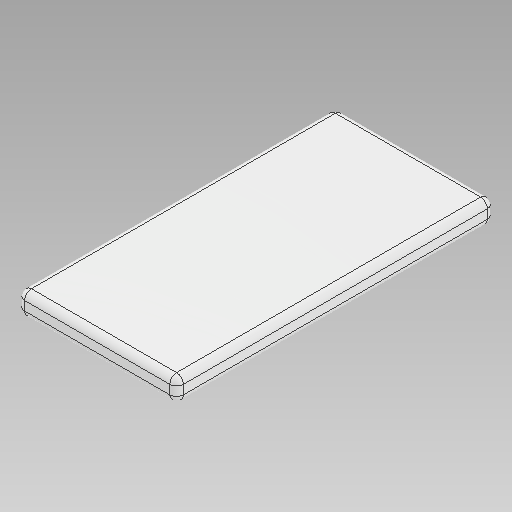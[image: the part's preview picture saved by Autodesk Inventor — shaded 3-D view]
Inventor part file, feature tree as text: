
AUTODESK INVENTOR PART (.ipt)
format: ipt  version: 2020 (Build 240168000, 168)  size: 187,904 bytes
history: native  units: in
note: dims shown in document units (in); Inventor stores cm internally (conversion verified against a paired STEP export)
features: extrude x1, fillet x1, sketch x1
ambient origin geometry x8: Origin, YZ Plane, XZ Plane, XY Plane, X Axis, Y Axis, Z Axis, Center Point
bodies: Solid1 (feature_tree)
feature tree (3):
  extrude  "Extrusion1"  Depth=5.5118in
  fillet  "Fillet1"  Radius=0.3937in
  sketch  "Sketch1"  dims[d0=2.7559in d1=5.5118in d2=0.3937in d3=0.0in d4=0.1181in]
